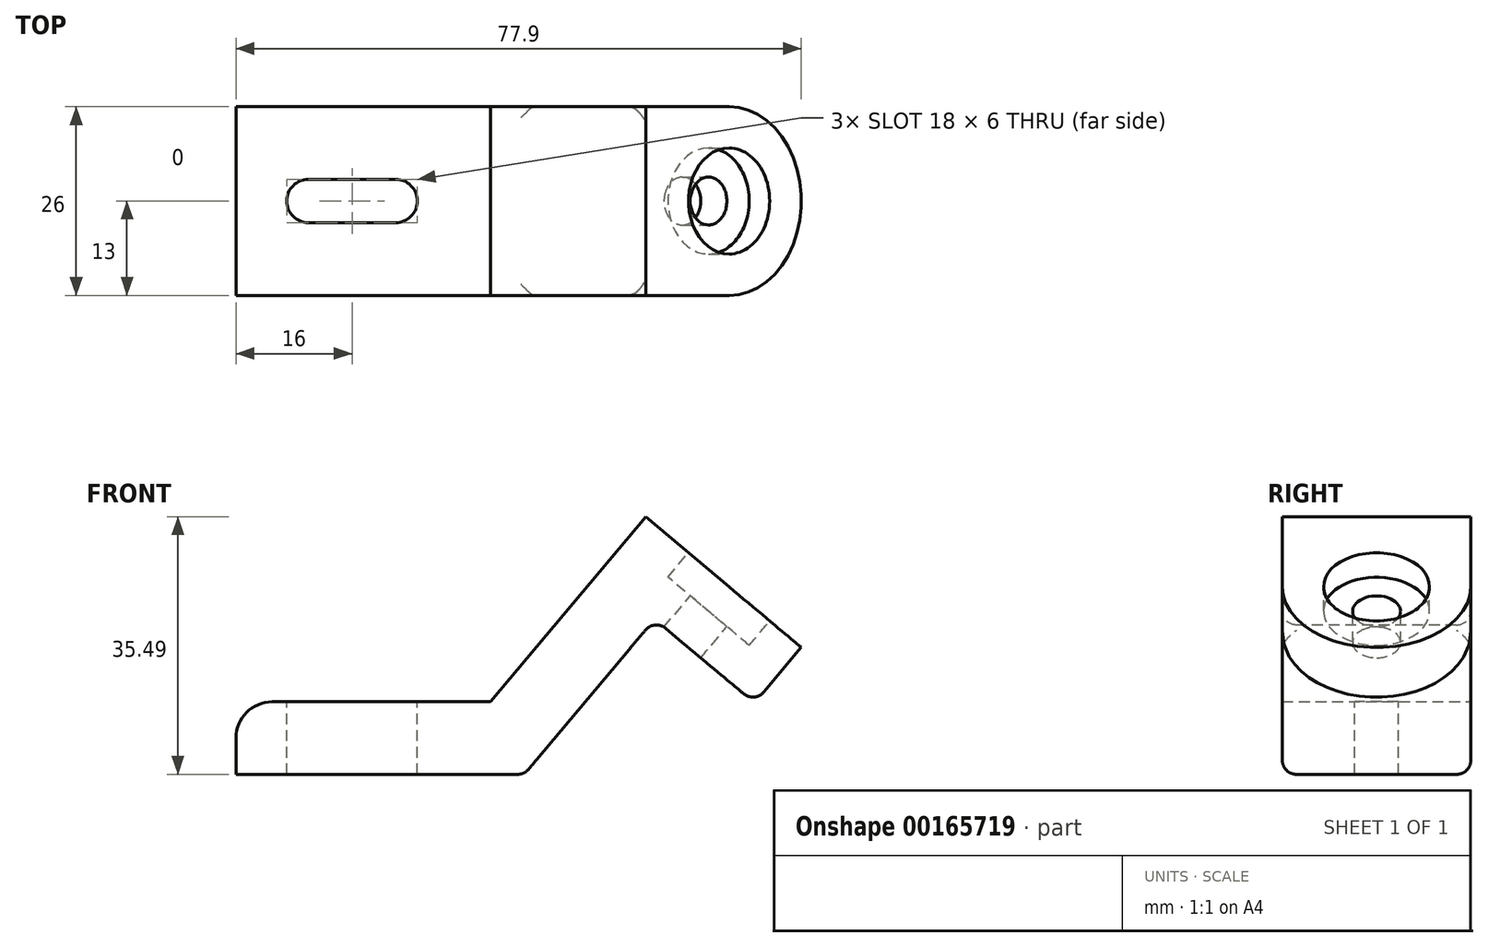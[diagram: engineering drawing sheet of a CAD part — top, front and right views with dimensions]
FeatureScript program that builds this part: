
annotation { "Feature Type Name" : "Feature", "Feature Type Description" : "" }
export const myFeature = defineFeature(function(context is Context, id is Id, definition is map)
    precondition{}
    {
        {
            var Q0;
            Q0=qCreatedBy(makeId("Front.planeOp"),FACE);
            var sketch = newSketch(context, id + "F0", { "sketchPlane" : qUnion([Q0])});
            skLineSegment(sketch, "E0", {"start": v(-38.8, 0) * mm, "end": v(0, 0) * mm});
            skLineSegment(sketch, "E1", {"start": v(0, 0) * mm, "end": v(18.64, 22.22) * mm});
            skLineSegment(sketch, "E2", {"start": v(18.64, 22.22) * mm, "end": v(33.96, 9.36) * mm});
            skLineSegment(sketch, "E3.0", {"start": v(17.65, 33.49) * mm, "end": v(39.1, 15.49) * mm});
            skLineSegment(sketch, "E3.1", {"start": v(-3.73, 8) * mm, "end": v(17.65, 33.49) * mm});
            skLineSegment(sketch, "E3.2", {"start": v(-38.8, 8) * mm, "end": v(-3.73, 8) * mm});
            skLineSegment(sketch, "E4.0", {"start": v(18.89, 19.4) * mm, "end": v(32.68, 7.83) * mm});
            skLineSegment(sketch, "E4.1", {"start": v(0.93, -2) * mm, "end": v(18.89, 19.4) * mm});
            skLineSegment(sketch, "E4.2", {"start": v(-38.8, -2) * mm, "end": v(0.93, -2) * mm});
            skLineSegment(sketch, "E5", {"start": v(-38.8, 8) * mm, "end": v(-38.8, -2) * mm});
            skLineSegment(sketch, "E6", {"start": v(39.1, 15.49) * mm, "end": v(32.68, 7.83) * mm});
            skSolve(sketch);
        }
        {
            var Q0;
            Q0 = qSketchRegion(id + "F0", true);
            extrude(context, id + "F1", {"entities" : qUnion([Q0]), "endBound" : BoundingType.SYMMETRIC, "depth" : 26 * mm});
        }
        {
            var Q0;
            Q0=makeQuery(id+"F1.opExtrude","CAP_EDGE",EDGE,{"disambiguationData":[OSD([sQuery(id+"F0.wireOp",EDGE,"E6")])],"isStart":false});
            var Q1;
            Q1=makeQuery(id+"F1.opExtrude","CAP_EDGE",EDGE,{"disambiguationData":[OSD([sQuery(id+"F0.wireOp",EDGE,"E6")])],"isStart":true});
            fillet(context, id + "F2", {"entities" : qUnion([Q0, Q1]), "radius" : 13 * mm, "tangentPropagation" : true, "allowEdgeOverflow" : false});
        }
        {
            var Q0;
            Q0=makeQuery(id+"F1.opExtrude","SWEPT_FACE",FACE,{"disambiguationData":[OSD([sQuery(id+"F0.wireOp",EDGE,"E4.0")])]});
            var Q1;
            Q1=makeQuery(id+"F1.opExtrude","SWEPT_EDGE",EDGE,{"disambiguationData":[OSD([sQuery(id+"F0.wireOp",EDGE,"E4.1"),sQuery(id+"F0.wireOp",EDGE,"E4.2")])]});
            var Q2;
            Q2=makeQuery(id+"F1.opExtrude","CAP_EDGE",EDGE,{"disambiguationData":[OSD([sQuery(id+"F0.wireOp",EDGE,"E4.2")])],"isStart":false});
            var Q3;
            Q3=makeQuery(id+"F1.opExtrude","CAP_EDGE",EDGE,{"disambiguationData":[OSD([sQuery(id+"F0.wireOp",EDGE,"E4.2")])],"isStart":true});
            fillet(context, id + "F3", {"entities" : qUnion([Q0, Q1, Q2, Q3]), "radius" : 2 * mm, "tangentPropagation" : true, "allowEdgeOverflow" : false});
        }
        {
            var Q0;
            Q0=makeQuery(id+"F1.opExtrude","SWEPT_FACE",FACE,{"disambiguationData":[OSD([sQuery(id+"F0.wireOp",EDGE,"E3.0")])]});
            var sketch = newSketch(context, id + "F4", { "sketchPlane" : qUnion([Q0])});
            skCircle(sketch, "E7", {"center": v(7, 0) * mm, "radius": 7.3 * mm});
            skSolve(sketch);
        }
        {
            var Q0;
            Q0 = qSketchRegion(id + "F4", true);
            extrude(context, id + "F5", {"entities" : qUnion([Q0]), "operationType" : NewBodyOperationType.REMOVE, "oppositeDirection" : true, "depth" : 4.4 * mm});
        }
        {
            var Q0;
            Q0=makeQuery(id+"F5.boolean.opBoolean","COPY",FACE,{"derivedFrom":makeQuery(id+"F5.opExtrude","CAP_FACE",FACE,{"disambiguationData":[OSD([sQuery(id+"F4.wireOp",EDGE,"E7")])],"isStart":false})});
            var sketch = newSketch(context, id + "F6", { "sketchPlane" : qUnion([Q0])});
            skCircle(sketch, "E8", {"center": v(7, 0) * mm, "radius": 3.3 * mm});
            skSolve(sketch);
        }
        {
            var Q0;
            Q0 = qSketchRegion(id + "F6", true);
            extrude(context, id + "F7", {"entities" : qUnion([Q0]), "operationType" : NewBodyOperationType.REMOVE, "endBound" : BoundingType.THROUGH_ALL, "oppositeDirection" : true, "depth" : 25 * mm});
        }
        {
            var Q0;
            Q0=makeQuery(id+"F1.opExtrude","SWEPT_FACE",FACE,{"disambiguationData":[OSD([sQuery(id+"F0.wireOp",EDGE,"E3.2")])]});
            var sketch = newSketch(context, id + "F8", { "sketchPlane" : qUnion([Q0])});
            skLineSegment(sketch, "E9", {"start": v(-28.8, 0) * mm, "end": v(-16.8, 0) * mm});
            skArc(sketch, "E10.0.startCap", {"start": v(-28.8, -3) * mm, "mid": v(-31.8, 0) * mm, "end": v(-28.8, 3) * mm});
            skArc(sketch, "E10.0.endCap", {"start": v(-16.8, 3) * mm, "mid": v(-13.8, 0) * mm, "end": v(-16.8, -3) * mm});
            skLineSegment(sketch, "E10.0.left", {"start": v(-28.8, 3) * mm, "end": v(-16.8, 3) * mm});
            skLineSegment(sketch, "E10.0.right", {"start": v(-28.8, -3) * mm, "end": v(-16.8, -3) * mm});
            skSolve(sketch);
        }
        {
            var Q0;
            Q0 = qSketchRegion(id + "F8", true);
            extrude(context, id + "F9", {"entities" : qUnion([Q0]), "operationType" : NewBodyOperationType.REMOVE, "endBound" : BoundingType.THROUGH_ALL, "oppositeDirection" : true, "depth" : 25 * mm});
        }
        {
            var Q0;
            Q0=makeQuery(id+"F1.opExtrude","SWEPT_EDGE",EDGE,{"disambiguationData":[OSD([sQuery(id+"F0.wireOp",EDGE,"E3.2"),sQuery(id+"F0.wireOp",EDGE,"E5")])]});
            fillet(context, id + "F10", {"entities" : qUnion([Q0]), "radius" : 5 * mm, "tangentPropagation" : true, "allowEdgeOverflow" : false});
        }
    });
